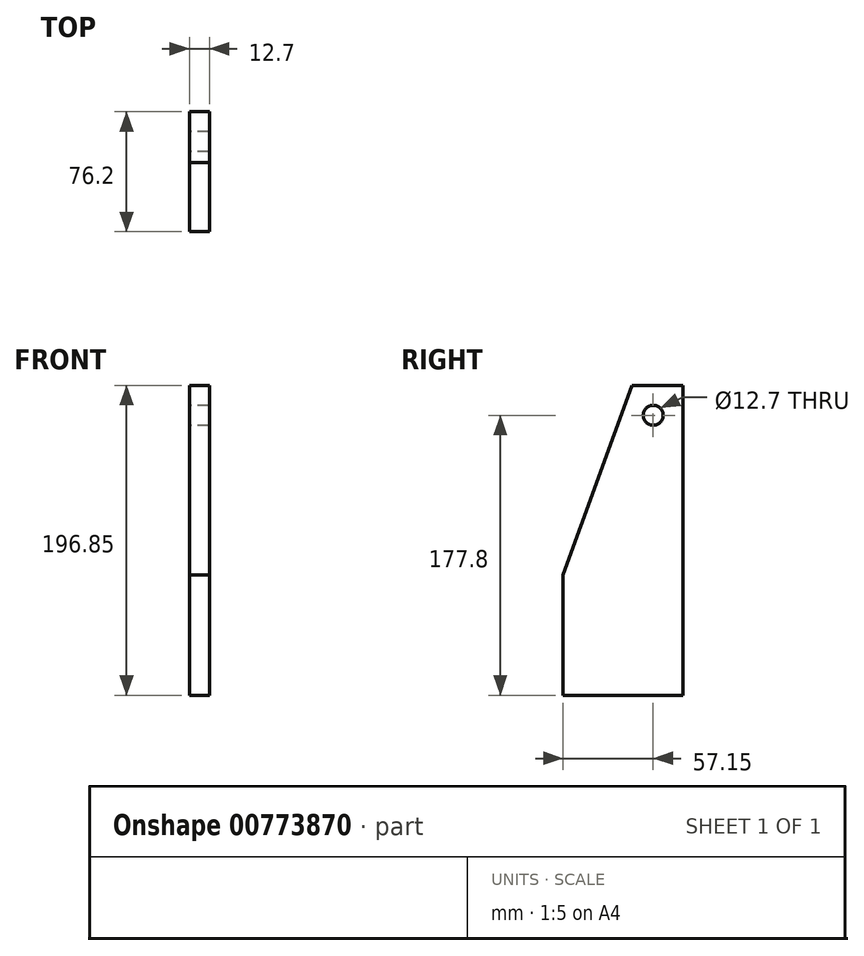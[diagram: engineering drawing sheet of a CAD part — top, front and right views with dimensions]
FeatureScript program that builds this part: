
annotation { "Feature Type Name" : "Feature", "Feature Type Description" : "" }
export const myFeature = defineFeature(function(context is Context, id is Id, definition is map)
    precondition{}
    {
        {
            var Q0;
            Q0=qCreatedBy(makeId("Right.planeOp"), FACE);
            var sketch = newSketch(context, id + "F0", { "sketchPlane" : qUnion([Q0])});
            skLineSegment(sketch, "E0", {"start": v(0, 0) * mm, "end": v(0, 177.8) * mm});
            skLineSegment(sketch, "E1", {"start": v(0, 0) * mm, "end": v(-76.2, 0) * mm});
            skLineSegment(sketch, "E2", {"start": v(-76.2, 0) * mm, "end": v(-76.2, 76.48) * mm});
            skLineSegment(sketch, "E3", {"start": v(-76.2, 76.48) * mm, "end": v(-36.95, 184.32) * mm});
            skArc(sketch, "E4", {"start": v(0, 177.8) * mm, "mid": v(-15.74, 196.56) * mm, "end": v(-36.95, 184.32) * mm});
            skCircle(sketch, "E5", {"center": v(-19.05, 177.8) * mm, "radius": 6.35 * mm});
            skLineSegment(sketch, "E6", {"start": v(-36.95, 184.32) * mm, "end": v(-32.39, 196.85) * mm});
            skLineSegment(sketch, "E7", {"start": v(-32.39, 196.85) * mm, "end": v(0, 196.85) * mm});
            skLineSegment(sketch, "E8", {"start": v(0, 196.85) * mm, "end": v(0, 177.8) * mm});
            skSolve(sketch);
        }
        {
            var Q0;
            Q0 = qSketchRegion(id + "F0", true);
            extrude(context, id + "F1", {"entities" : qUnion([Q0]), "depth" : 12.7 * mm, "offsetDistance" : 25.4 * mm});
        }
    });
